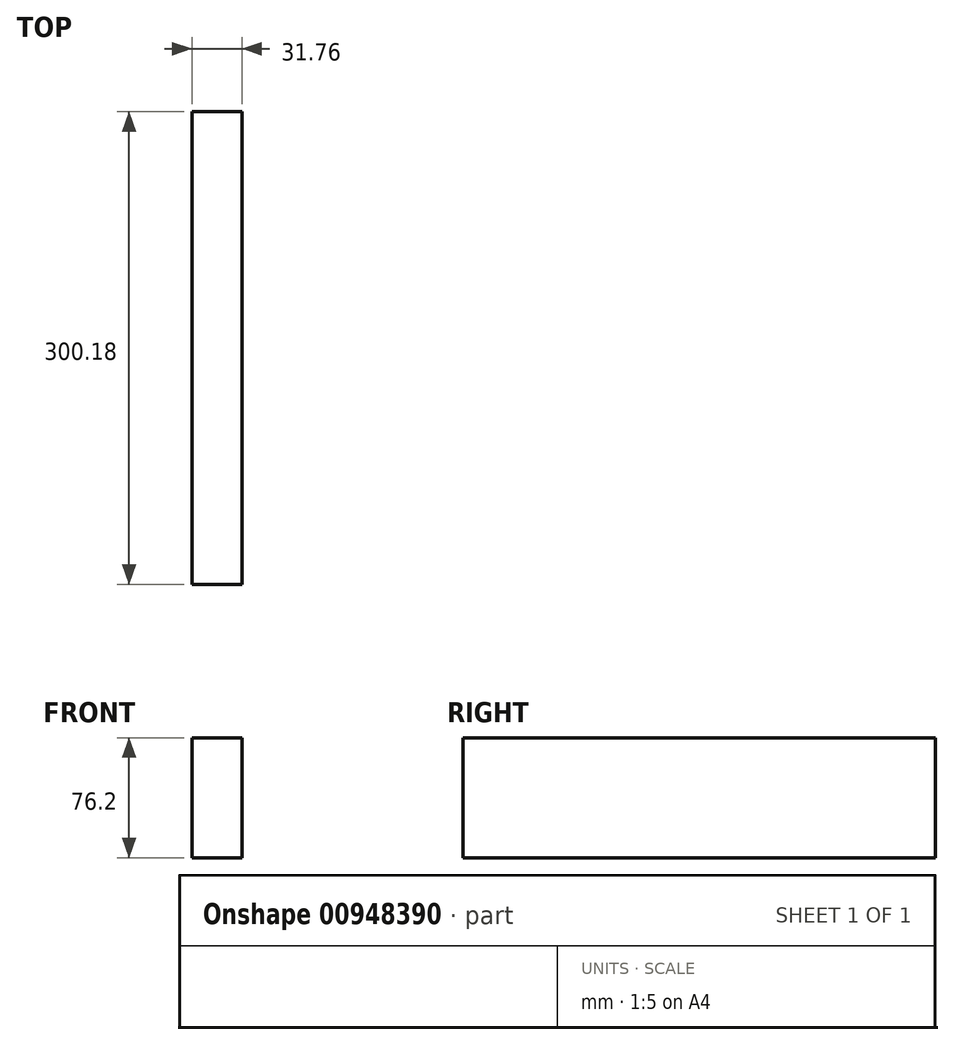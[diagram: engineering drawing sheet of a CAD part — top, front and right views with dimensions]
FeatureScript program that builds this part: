
annotation { "Feature Type Name" : "Feature", "Feature Type Description" : "" }
export const myFeature = defineFeature(function(context is Context, id is Id, definition is map)
    precondition{}
    {
        {
            var Q0;
            Q0=qCreatedBy(makeId("Top.planeOp"),FACE);
            var sketch = newSketch(context, id + "F0", { "sketchPlane" : qUnion([Q0])});
            skLineSegment(sketch, "E0.bottom", {"start": v(-15.88, 150.09) * mm, "end": v(15.88, 150.09) * mm});
            skLineSegment(sketch, "E0.top", {"start": v(-15.88, -150.09) * mm, "end": v(15.88, -150.09) * mm});
            skLineSegment(sketch, "E0.left", {"start": v(-15.87, 150.09) * mm, "end": v(-15.88, -150.09) * mm});
            skLineSegment(sketch, "E0.right", {"start": v(15.88, 150.09) * mm, "end": v(15.87, -150.09) * mm});
            skSolve(sketch);
        }
        {
            var Q0;
            Q0=makeQuery(id+"F0.imprint","IMPRINT",FACE,{"disambiguationData":[TD([[makeQuery(id+"F0.imprint","IMPRINT",EDGE,{"derivedFrom":sQuery(id+"F0.wireOp",EDGE,"E0.bottom")}),-1.0]])]});
            extrude(context, id + "F1", {"entities" : qUnion([Q0]), "depth" : 76.2 * mm, "offsetDistance" : 25.4 * mm});
        }
    });
